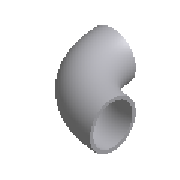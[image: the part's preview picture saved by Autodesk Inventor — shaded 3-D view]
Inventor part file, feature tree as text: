
AUTODESK INVENTOR PART (.ipt)
format: ipt  version: 2023.1 (Build 271208000, 208)  size: 183,296 bytes
history: native  units: mm (DEFAULTED — no unit token found)
features: other x4, sketch x2, sweep x1
ambient origin geometry x8: Origin, YZ Plane, XZ Plane, XY Plane, X Axis, Y Axis, Z Axis, Center Point
bodies: Solid1 (feature_tree)
feature tree (7):
  sweep  "Sweep1"
  other  "Work Point1"
  other  "Work Point2"
  other  "Work Axis1"
  other  "Work Axis2"
  sketch  "Sketch1"  dims[d0=109.1mm d1=114.3mm]
  sketch  "Sketch2"  dims[d2=152.0mm d3=152.0mm d4=0.0mm d5=0.0mm]
